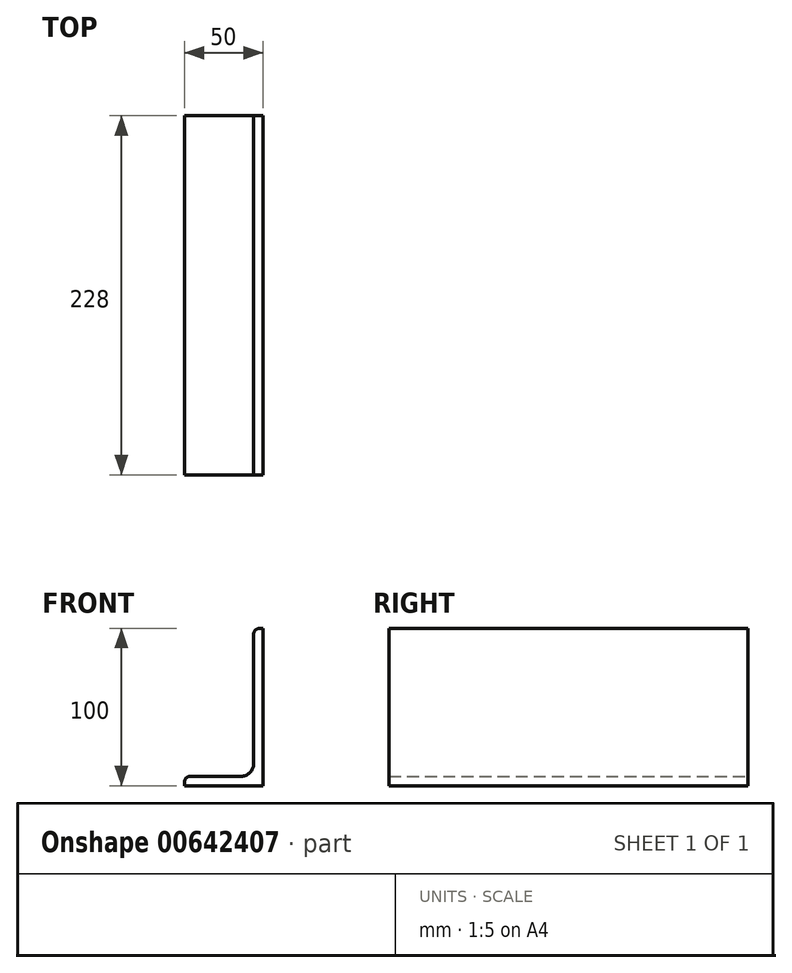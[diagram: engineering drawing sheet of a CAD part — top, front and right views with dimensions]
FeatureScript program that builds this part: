
annotation { "Feature Type Name" : "Feature", "Feature Type Description" : "" }
export const myFeature = defineFeature(function(context is Context, id is Id, definition is map)
    precondition{}
    {
        {
            var Q0;
            Q0=qCreatedBy(makeId("Front.planeOp"),FACE);
            var sketch = newSketch(context, id + "F0", { "sketchPlane" : qUnion([Q0])});
            skLineSegment(sketch, "E0", {"start": v(0, 0) * mm, "end": v(50, 0) * mm});
            skLineSegment(sketch, "E1", {"start": v(50, 0) * mm, "end": v(50, 100) * mm});
            skLineSegment(sketch, "E2.0", {"start": v(44, 14) * mm, "end": v(44, 96) * mm});
            skLineSegment(sketch, "E2.1", {"start": v(4, 6) * mm, "end": v(36, 6) * mm});
            skLineSegment(sketch, "E3", {"start": v(0, 0) * mm, "end": v(0, 2) * mm});
            skLineSegment(sketch, "E4", {"start": v(50, 100) * mm, "end": v(48, 100) * mm});
            skPoint(sketch, "E5.visualSharp", {"position": v(44, 100) * mm});
            skArc(sketch, "E5.filletArc", {"start": v(48, 100) * mm, "mid": v(45.17, 98.83) * mm, "end": v(44, 96) * mm});
            skPoint(sketch, "E6.visualSharp", {"position": v(0, 6) * mm});
            skArc(sketch, "E6.filletArc", {"start": v(4, 6) * mm, "mid": v(1.17, 4.83) * mm, "end": v(0, 2) * mm});
            skPoint(sketch, "E7.visualSharp", {"position": v(44, 6) * mm});
            skArc(sketch, "E7.filletArc", {"start": v(36, 6) * mm, "mid": v(41.66, 8.34) * mm, "end": v(44, 14) * mm});
            skSolve(sketch);
        }
        {
            var Q0;
            Q0=makeQuery(id+"F0.imprint","IMPRINT",FACE,{"disambiguationData":[TD([[makeQuery(id+"F0.imprint","IMPRINT",EDGE,{"derivedFrom":sQuery(id+"F0.wireOp",EDGE,"E0")}),1.0]])]});
            extrude(context, id + "F1", {"entities" : qUnion([Q0]), "depth" : 228 * mm, "offsetDistance" : 25 * mm});
        }
    });
